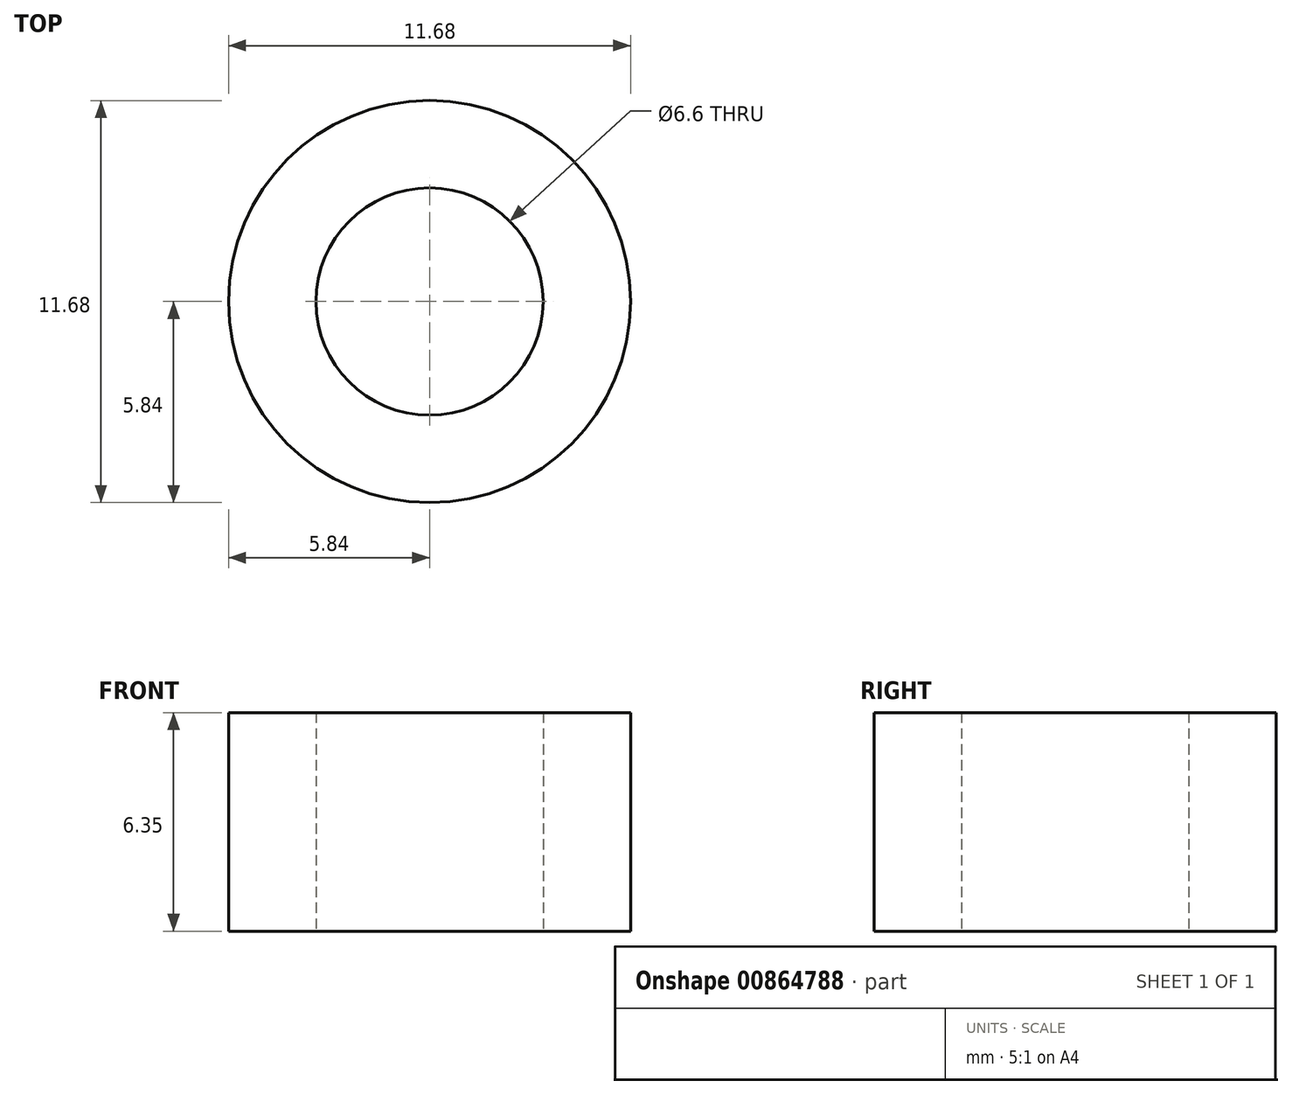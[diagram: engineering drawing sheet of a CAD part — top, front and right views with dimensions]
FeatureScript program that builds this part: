
annotation { "Feature Type Name" : "Feature", "Feature Type Description" : "" }
export const myFeature = defineFeature(function(context is Context, id is Id, definition is map)
    precondition{}
    {
        {
            var Q0;
            Q0=qCreatedBy(makeId("Top.planeOp"),FACE);
            var sketch = newSketch(context, id + "F0", { "sketchPlane" : qUnion([Q0])});
            skCircle(sketch, "E0", {"center": v(0, 0) * mm, "radius": 3.3 * mm});
            skCircle(sketch, "E1", {"center": v(0, 0) * mm, "radius": 5.84 * mm});
            skSolve(sketch);
        }
        {
            var Q0;
            Q0=makeQuery(id+"F0.imprint","IMPRINT",FACE,{"disambiguationData":[TD([[makeQuery(id+"F0.imprint","IMPRINT",EDGE,{"derivedFrom":sQuery(id+"F0.wireOp",EDGE,"E0")}),-1.0]])]});
            extrude(context, id + "F1", {"entities" : qUnion([Q0]), "depth" : 6.35 * mm, "offsetDistance" : 25.4 * mm});
        }
    });
